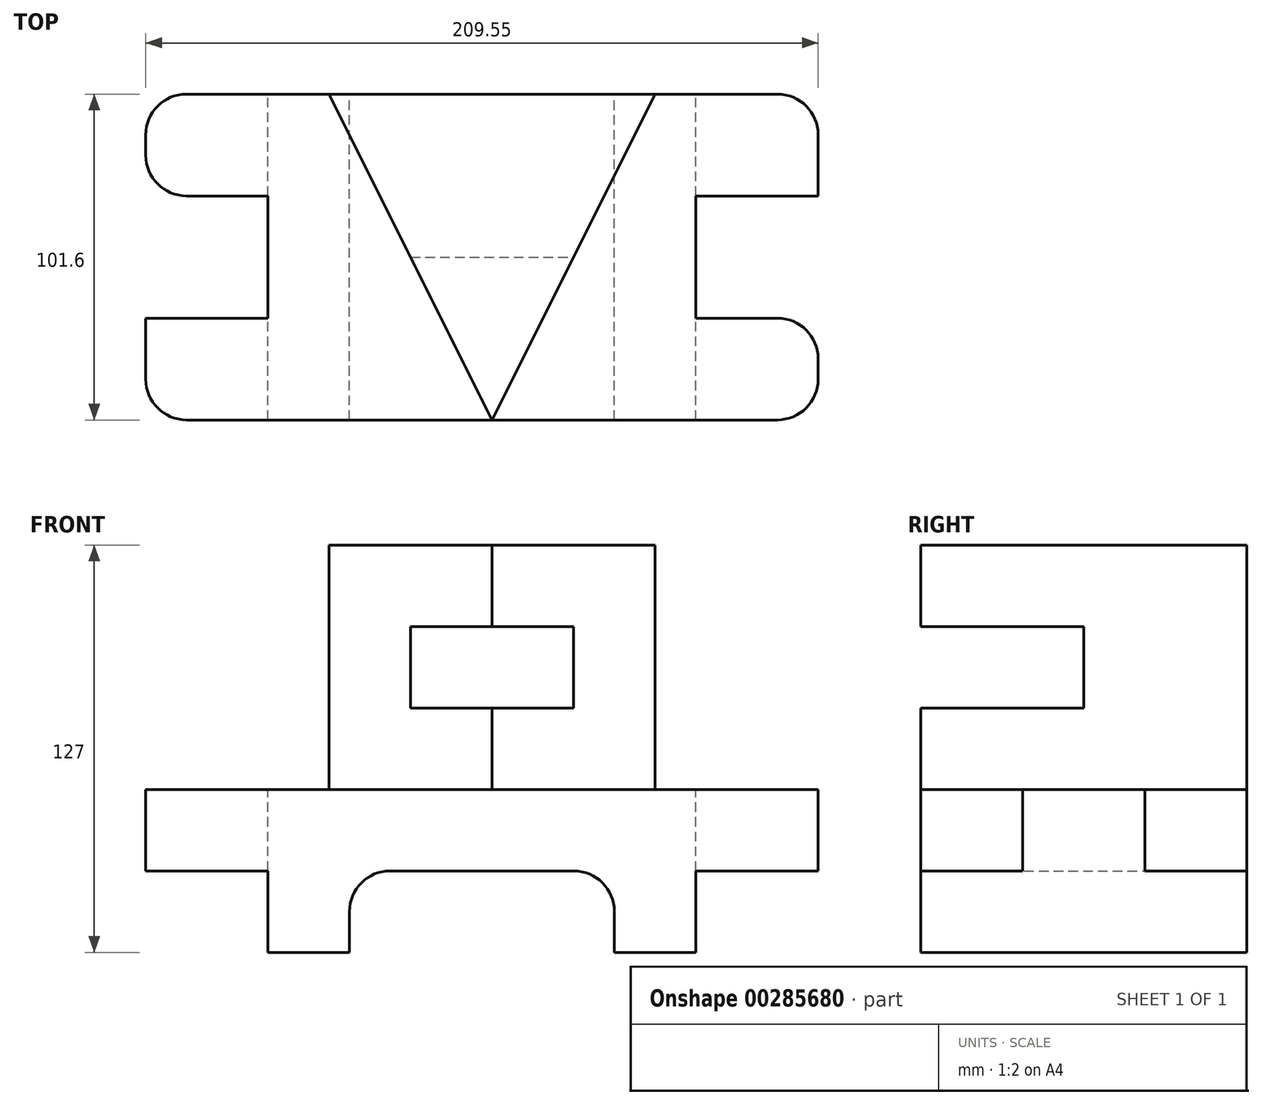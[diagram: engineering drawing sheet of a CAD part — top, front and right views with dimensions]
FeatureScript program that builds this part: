
annotation { "Feature Type Name" : "Feature", "Feature Type Description" : "" }
export const myFeature = defineFeature(function(context is Context, id is Id, definition is map)
    precondition{}
    {
        {
            var Q0;
            Q0=qCreatedBy(makeId("Front.planeOp"),FACE);
            var sketch = newSketch(context, id + "F0", { "sketchPlane" : qUnion([Q0])});
            skLineSegment(sketch, "E0", {"start": v(0, 0) * mm, "end": v(0, 25.4) * mm});
            skLineSegment(sketch, "E1", {"start": v(0, 25.4) * mm, "end": v(209.55, 25.4) * mm});
            skLineSegment(sketch, "E2", {"start": v(209.55, 25.4) * mm, "end": v(209.55, 0) * mm});
            skLineSegment(sketch, "E3", {"start": v(209.55, 0) * mm, "end": v(0, 0) * mm});
            skSolve(sketch);
        }
        {
            var Q0;
            Q0=makeQuery(id+"F0.imprint","IMPRINT",FACE,{"disambiguationData":[TD([[makeQuery(id+"F0.imprint","IMPRINT",EDGE,{"derivedFrom":sQuery(id+"F0.wireOp",EDGE,"E0")}),-1.0]])]});
            extrude(context, id + "F1", {"entities" : qUnion([Q0]), "depth" : 101.6 * mm});
        }
        {
            var Q0;
            Q0=makeQuery(id+"F1.opExtrude","SWEPT_FACE",FACE,{"disambiguationData":[OSD([sQuery(id+"F0.wireOp",EDGE,"E1")])]});
            var sketch = newSketch(context, id + "F2", { "sketchPlane" : qUnion([Q0])});
            skLineSegment(sketch, "E4.bottom", {"start": v(209.55, -31.75) * mm, "end": v(171.45, -31.75) * mm});
            skLineSegment(sketch, "E4.top", {"start": v(209.55, -69.85) * mm, "end": v(171.45, -69.85) * mm});
            skLineSegment(sketch, "E4.left", {"start": v(209.55, -31.75) * mm, "end": v(209.55, -69.85) * mm});
            skLineSegment(sketch, "E4.right", {"start": v(171.45, -31.75) * mm, "end": v(171.45, -69.85) * mm});
            skLineSegment(sketch, "E5.bottom", {"start": v(0, -31.75) * mm, "end": v(38.1, -31.75) * mm});
            skLineSegment(sketch, "E5.top", {"start": v(0, -69.85) * mm, "end": v(38.1, -69.85) * mm});
            skLineSegment(sketch, "E5.left", {"start": v(0, -31.75) * mm, "end": v(0, -69.85) * mm});
            skLineSegment(sketch, "E5.right", {"start": v(38.1, -31.75) * mm, "end": v(38.1, -69.85) * mm});
            skSolve(sketch);
        }
        {
            var Q0;
            Q0=makeQuery(id+"F2.imprint","IMPRINT",FACE,{"disambiguationData":[TD([[makeQuery(id+"F2.imprint","IMPRINT",EDGE,{"derivedFrom":sQuery(id+"F2.wireOp",EDGE,"E5.bottom")}),-1.0]])]});
            var Q1;
            Q1=makeQuery(id+"F2.imprint","IMPRINT",FACE,{"disambiguationData":[TD([[makeQuery(id+"F2.imprint","IMPRINT",EDGE,{"derivedFrom":sQuery(id+"F2.wireOp",EDGE,"E4.bottom")}),1.0]])]});
            extrude(context, id + "F3", {"entities" : qUnion([Q0, Q1]), "operationType" : NewBodyOperationType.REMOVE, "endBound" : BoundingType.THROUGH_ALL, "oppositeDirection" : true, "depth" : 25.4 * mm});
        }
        {
            var Q0;
            Q0=makeQuery(id+"F1.opExtrude","SWEPT_FACE",FACE,{"disambiguationData":[OSD([sQuery(id+"F0.wireOp",EDGE,"E3")])]});
            var sketch = newSketch(context, id + "F4", { "sketchPlane" : qUnion([Q0])});
            skLineSegment(sketch, "E6.bottom", {"start": v(38.1, 101.6) * mm, "end": v(171.45, 101.6) * mm});
            skLineSegment(sketch, "E6.top", {"start": v(38.1, 0) * mm, "end": v(171.45, 0) * mm});
            skLineSegment(sketch, "E6.left", {"start": v(38.1, 101.6) * mm, "end": v(38.1, 0) * mm});
            skLineSegment(sketch, "E6.right", {"start": v(171.45, 101.6) * mm, "end": v(171.45, 0) * mm});
            skSolve(sketch);
        }
        {
            var Q0;
            {var subQ7=sQuery(id+"F4.wireOp",EDGE,"E6.bottom");Q0=makeQuery(id+"F4.imprint","IMPRINT",FACE,{"disambiguationData":[TD([[makeQuery(id+"F4.imprint","IMPRINT",EDGE,{"derivedFrom":subQ7}),1.0]])]});}
            extrude(context, id + "F5", {"entities" : qUnion([Q0]), "operationType" : NewBodyOperationType.ADD, "depth" : 25.4 * mm});
        }
        {
            var Q0;
            Q0=makeQuery(id+"F5.opExtrude","CAP_FACE",FACE,{"disambiguationData":[OSD([sQuery(id+"F4.wireOp",EDGE,"E6.bottom"),sQuery(id+"F4.wireOp",EDGE,"E6.top"),sQuery(id+"F4.wireOp",EDGE,"E6.left"),sQuery(id+"F4.wireOp",EDGE,"E6.right")])],"isStart":false});
            var sketch = newSketch(context, id + "F6", { "sketchPlane" : qUnion([Q0])});
            skLineSegment(sketch, "E7.bottom", {"start": v(63.5, 101.6) * mm, "end": v(146.05, 101.6) * mm});
            skLineSegment(sketch, "E7.top", {"start": v(63.5, 0) * mm, "end": v(146.05, 0) * mm});
            skLineSegment(sketch, "E7.left", {"start": v(63.5, 101.6) * mm, "end": v(63.5, 0) * mm});
            skLineSegment(sketch, "E7.right", {"start": v(146.05, 101.6) * mm, "end": v(146.05, 0) * mm});
            skSolve(sketch);
        }
        {
            var Q0;
            Q0=makeQuery(id+"F6.imprint","IMPRINT",FACE,{"disambiguationData":[TD([[makeQuery(id+"F6.imprint","IMPRINT",EDGE,{"derivedFrom":sQuery(id+"F6.wireOp",EDGE,"E7.bottom")}),1.0]])]});
            extrude(context, id + "F7", {"entities" : qUnion([Q0]), "operationType" : NewBodyOperationType.REMOVE, "oppositeDirection" : true, "depth" : 25.4 * mm});
        }
        {
            var Q0;
            Q0=makeQuery(id+"F1.opExtrude","SWEPT_FACE",FACE,{"disambiguationData":[OSD([sQuery(id+"F0.wireOp",EDGE,"E1")])]});
            var sketch = newSketch(context, id + "F8", { "sketchPlane" : qUnion([Q0])});
            skLineSegment(sketch, "E8", {"start": v(57.15, 0) * mm, "end": v(158.75, 0) * mm});
            skLineSegment(sketch, "E9", {"start": v(158.75, 0) * mm, "end": v(107.95, -101.6) * mm});
            skLineSegment(sketch, "E10", {"start": v(107.95, -101.6) * mm, "end": v(57.15, 0) * mm});
            skSolve(sketch);
        }
        {
            var Q0;
            Q0=makeQuery(id+"F8.imprint","IMPRINT",FACE,{"disambiguationData":[TD([[makeQuery(id+"F8.imprint","IMPRINT",EDGE,{"derivedFrom":sQuery(id+"F8.wireOp",EDGE,"E8")}),-1.0]])]});
            extrude(context, id + "F9", {"entities" : qUnion([Q0]), "operationType" : NewBodyOperationType.ADD, "depth" : 76.2 * mm});
        }
        {
            var Q0;
            Q0=makeQuery(id+"F5.boolean.opBoolean","MERGE",FACE,{"derivedFrom":[makeQuery(id+"F1.opExtrude","CAP_FACE",FACE,{"disambiguationData":[OSD([sQuery(id+"F0.wireOp",EDGE,"E0"),sQuery(id+"F0.wireOp",EDGE,"E1"),sQuery(id+"F0.wireOp",EDGE,"E2"),sQuery(id+"F0.wireOp",EDGE,"E3")])],"isStart":false}),makeQuery(id+"F5.opExtrude","SWEPT_FACE",FACE,{"disambiguationData":[OSD([sQuery(id+"F4.wireOp",EDGE,"E6.bottom")])]})]});
            var sketch = newSketch(context, id + "F10", { "sketchPlane" : qUnion([Q0])});
            skLineSegment(sketch, "E11", {"start": v(82.55, 76.2) * mm, "end": v(133.35, 76.2) * mm});
            skLineSegment(sketch, "E12", {"start": v(133.35, 76.2) * mm, "end": v(133.35, 50.8) * mm});
            skLineSegment(sketch, "E13", {"start": v(133.35, 50.8) * mm, "end": v(82.55, 50.8) * mm});
            skLineSegment(sketch, "E14", {"start": v(82.55, 50.8) * mm, "end": v(82.55, 76.2) * mm});
            skSolve(sketch);
        }
        {
            var Q0;
            Q0=makeQuery(id+"F10.imprint","IMPRINT",FACE,{"disambiguationData":[TD([[makeQuery(id+"F10.imprint","IMPRINT",EDGE,{"derivedFrom":sQuery(id+"F10.wireOp",EDGE,"E11")}),-1.0]])]});
            extrude(context, id + "F11", {"entities" : qUnion([Q0]), "operationType" : NewBodyOperationType.REMOVE, "oppositeDirection" : true, "depth" : 50.8 * mm});
        }
        {
            var Q0;
            Q0=makeQuery(id+"F1.opExtrude","CAP_EDGE",EDGE,{"disambiguationData":[OSD([sQuery(id+"F0.wireOp",EDGE,"E0")])],"isStart":false});
            var Q1;
            Q1=makeQuery(id+"F3.boolean.opBoolean","COPY",EDGE,{"derivedFrom":makeQuery(id+"F3.opExtrude","SWEPT_EDGE",EDGE,{"disambiguationData":[OSD([sQuery(id+"F0.wireOp",EDGE,"E0"),sQuery(id+"F0.wireOp",EDGE,"E1"),sQuery(id+"F2.wireOp",EDGE,"E5.top"),sQuery(id+"F2.wireOp",EDGE,"E5.left")])]})});
            var Q2;
            Q2=makeQuery(id+"F3.boolean.opBoolean","COPY",EDGE,{"derivedFrom":makeQuery(id+"F3.opExtrude","SWEPT_EDGE",EDGE,{"disambiguationData":[OSD([sQuery(id+"F0.wireOp",EDGE,"E0"),sQuery(id+"F0.wireOp",EDGE,"E1"),sQuery(id+"F2.wireOp",EDGE,"E5.bottom"),sQuery(id+"F2.wireOp",EDGE,"E5.left")])]})});
            var Q3;
            Q3=makeQuery(id+"F1.opExtrude","CAP_EDGE",EDGE,{"disambiguationData":[OSD([sQuery(id+"F0.wireOp",EDGE,"E0")])],"isStart":true});
            var Q4;
            Q4=makeQuery(id+"F1.opExtrude","CAP_EDGE",EDGE,{"disambiguationData":[OSD([sQuery(id+"F0.wireOp",EDGE,"E2")])],"isStart":true});
            var Q5;
            Q5=makeQuery(id+"F3.boolean.opBoolean","COPY",EDGE,{"derivedFrom":makeQuery(id+"F3.opExtrude","SWEPT_EDGE",EDGE,{"disambiguationData":[OSD([sQuery(id+"F0.wireOp",EDGE,"E1"),sQuery(id+"F0.wireOp",EDGE,"E2"),sQuery(id+"F2.wireOp",EDGE,"E4.bottom"),sQuery(id+"F2.wireOp",EDGE,"E4.left")])]})});
            var Q6;
            Q6=makeQuery(id+"F3.boolean.opBoolean","COPY",EDGE,{"derivedFrom":makeQuery(id+"F3.opExtrude","SWEPT_EDGE",EDGE,{"disambiguationData":[OSD([sQuery(id+"F0.wireOp",EDGE,"E1"),sQuery(id+"F0.wireOp",EDGE,"E2"),sQuery(id+"F2.wireOp",EDGE,"E4.top"),sQuery(id+"F2.wireOp",EDGE,"E4.left")])]})});
            var Q7;
            Q7=makeQuery(id+"F1.opExtrude","CAP_EDGE",EDGE,{"disambiguationData":[OSD([sQuery(id+"F0.wireOp",EDGE,"E2")])],"isStart":false});
            var Q8;
            Q8=makeQuery(id+"F7.boolean.opBoolean","COPY",EDGE,{"derivedFrom":makeQuery(id+"F7.opExtrude","CAP_EDGE",EDGE,{"disambiguationData":[OSD([sQuery(id+"F6.wireOp",EDGE,"E7.left")])],"isStart":false})});
            var Q9;
            Q9=makeQuery(id+"F7.boolean.opBoolean","COPY",EDGE,{"derivedFrom":makeQuery(id+"F7.opExtrude","CAP_EDGE",EDGE,{"disambiguationData":[OSD([sQuery(id+"F6.wireOp",EDGE,"E7.right")])],"isStart":false})});
            fillet(context, id + "F12", {"entities" : qUnion([Q0, Q1, Q2, Q3, Q4, Q5, Q6, Q7, Q8, Q9]), "radius" : 12.7 * mm, "tangentPropagation" : true, "allowEdgeOverflow" : false});
        }
    });
